# Revit family: Heater-QMARK-QWD_Series-Washdown_Corrosion_Resistant_Unit_Gen2
name_source: partatom
category: Mechanical Equipment
units: mm (PartAtom-declared; Revit-internal decimal feet)

## family parameters
Cut with Voids When Loaded = No
Host = Face
OmniClass Number = 23.75.70.17.34
OmniClass Title = Unit Heaters
Part Type = Normal
Room Calculation Point = No
Round Connector Dimension = Use Diameter
Shared = No

## types (51) — shared parameters
Apparent Load = 0 VA
Bracket = Paint - Beige
Clearance from Ceiling = 0' - 9"
Clearance from Floor = 0' - 7"
Default Elevation = 4' - 0"
Description = Corrosion Resistant Unit Heaters
Drum = Paint - Beige
Frequency = 60 Hz
Instruction Sheet Link = https://www.marleymep.com
Manufacturer = Marley® Engineered Products
Number of Poles = 1
Power Factor = 1
Product Documentation Link = https://www.marleymep.com
Product Name = QWD Series - Washdown Corrosion-Resistant Unit Heater Gen2
Product Page URL = https://www.marleymep.com
URL = https://www.marleymep.com
Version = 2020 - v1.0a
Wall Clearance = 0' - 8"
Wall Mounted Offset = 0' - 6 13/16"

## per-type parameters (varying)
| type | 2-Stage Control | Actual Supply Air Flow | Air Flow - Throw | Amps | Drum Radius | Height CM | Height WM | Motor HP | Nema Box Height | Offset From Wall | Phase | Total Heating Capacity | Voltage | Wall Mount Nema Box Offset | Watts |
| QWD02112 |  | 700 CFM | 0' - 0" | 17 A | 0' - 6 1/2" | 1' - 8 31/32" | 1' - 8 31/32" |  | 0' - 6 1/4" | 0' - 6 3/8" | 1 | 6824.0 Btu/h | 120 V | 0' - 3 25/32" | 2000 W |
| QWD02812 |  | 700 CFM | 0' - 0" | 10 A | 0' - 6 1/2" | 1' - 8 31/32" | 1' - 8 31/32" |  | 0' - 6 1/4" | 0' - 6 3/8" | 1 | 6824.0 Btu/h | 208 V | 0' - 3 25/32" | 2000 W |
| QWD02212 |  | 700 CFM | 0' - 0" | 8 A | 0' - 6 1/2" | 1' - 8 31/32" | 1' - 8 31/32" |  | 0' - 6 1/4" | 0' - 6 3/8" | 1 | 6824.0 Btu/h | 240 V | 0' - 3 25/32" | 2000 W |
| QWD03112 |  | 700 CFM | 0' - 0" | 25 A | 0' - 6 1/2" | 1' - 8 31/32" | 1' - 8 31/32" |  | 0' - 6 1/4" | 0' - 6 3/8" | 1 | 10236.0 Btu/h | 120 V | 0' - 3 25/32" | 3000 W |
| QWD03812 |  | 700 CFM | 0' - 0" | 14 A | 0' - 6 1/2" | 1' - 8 31/32" | 1' - 8 31/32" |  | 0' - 6 1/4" | 0' - 6 3/8" | 1 | 10236.0 Btu/h | 208 V | 0' - 3 25/32" | 3000 W |
| QWD03212 |  | 700 CFM | 0' - 0" | 13 A | 0' - 6 1/2" | 1' - 8 31/32" | 1' - 8 31/32" |  | 0' - 6 1/4" | 0' - 6 3/8" | 1 | 10236.0 Btu/h | 240 V | 0' - 3 25/32" | 3000 W |
| QWD03712 |  | 700 CFM | 0' - 0" | 11 A | 0' - 6 1/2" | 1' - 8 31/32" | 1' - 8 31/32" |  | 0' - 6 1/4" | 0' - 6 3/8" | 1 | 10236.0 Btu/h | 277 V | 0' - 3 25/32" | 3000 W |
| QWD03832 |  | 700 CFM | 0' - 0" | 8 A | 0' - 6 1/2" | 1' - 8 31/32" | 1' - 8 31/32" |  | 0' - 6 1/4" | 0' - 6 3/8" | 3 | 10236.0 Btu/h | 208 V | 0' - 3 25/32" | 3000 W |
| QWD03232 |  | 700 CFM | 0' - 0" | 7 A | 0' - 6 1/2" | 1' - 8 31/32" | 1' - 8 31/32" |  | 0' - 6 1/4" | 0' - 6 3/8" | 3 | 10236.0 Btu/h | 240 V | 0' - 3 25/32" | 3000 W |
| QWD03432 |  | 700 CFM | 0' - 0" | 4 A | 0' - 6 1/2" | 1' - 8 31/32" | 1' - 8 31/32" |  | 0' - 6 1/4" | 0' - 6 3/8" | 3 | 10236.0 Btu/h | 480 V | 0' - 3 25/32" | 3000 W |
| QWD05812 |  | 700 CFM | 0' - 0" | 24 A | 0' - 6 1/2" | 1' - 8 31/32" | 1' - 8 31/32" |  | 0' - 6 1/4" | 0' - 6 3/8" | 1 | 17060.0 Btu/h | 208 V | 0' - 3 25/32" | 5000 W |
| QWD05212 |  | 700 CFM | 0' - 0" | 21 A | 0' - 6 1/2" | 1' - 8 31/32" | 1' - 8 31/32" |  | 0' - 6 1/4" | 0' - 6 3/8" | 1 | 17060.0 Btu/h | 240 V | 0' - 3 25/32" | 5000 W |
| QWD05712 |  | 700 CFM | 0' - 0" | 18 A | 0' - 6 1/2" | 1' - 8 31/32" | 1' - 8 31/32" |  | 0' - 6 1/4" | 0' - 6 3/8" | 1 | 17060.0 Btu/h | 277 V | 0' - 3 25/32" | 5000 W |
| QWD05412 |  | 700 CFM | 0' - 0" | 10 A | 0' - 6 1/2" | 1' - 8 31/32" | 1' - 8 31/32" |  | 0' - 6 1/4" | 0' - 6 3/8" | 1 | 17060.0 Btu/h | 480 V | 0' - 3 25/32" | 5000 W |
| QWD05832 |  | 700 CFM | 0' - 0" | 14 A | 0' - 6 1/2" | 1' - 8 31/32" | 1' - 8 31/32" |  | 0' - 6 1/4" | 0' - 6 3/8" | 3 | 17060.0 Btu/h | 208 V | 0' - 3 25/32" | 5000 W |
| QWD05232 |  | 700 CFM | 0' - 0" | 12 A | 0' - 6 1/2" | 1' - 8 31/32" | 1' - 8 31/32" |  | 0' - 6 1/4" | 0' - 6 3/8" | 3 | 17060.0 Btu/h | 240 V | 0' - 3 25/32" | 5000 W |
| QWD05432 |  | 700 CFM | 0' - 0" | 6 A | 0' - 6 1/2" | 1' - 8 31/32" | 1' - 8 31/32" |  | 0' - 6 1/4" | 0' - 6 3/8" | 3 | 17060.0 Btu/h | 480 V | 0' - 3 25/32" | 5000 W |
| QWD07812 |  | 700 CFM | 0' - 0" | 36 A | 0' - 6 1/2" | 1' - 8 31/32" | 1' - 8 31/32" |  | 0' - 6 1/4" | 0' - 6 3/8" | 1 | 25590.0 Btu/h | 208 V | 0' - 3 25/32" | 7500 W |
| QWD07212 |  | 700 CFM | 0' - 0" | 31 A | 0' - 6 1/2" | 1' - 8 31/32" | 1' - 8 31/32" |  | 0' - 6 1/4" | 0' - 6 3/8" | 1 | 25590.0 Btu/h | 240 V | 0' - 3 25/32" | 7500 W |
| QWD07712 |  | 700 CFM | 0' - 0" | 27 A | 0' - 6 1/2" | 1' - 8 31/32" | 1' - 8 31/32" |  | 0' - 6 1/4" | 0' - 6 3/8" | 1 | 25590.0 Btu/h | 277 V | 0' - 3 25/32" | 7500 W |
| QWD07412 |  | 700 CFM | 0' - 0" | 16 A | 0' - 6 1/2" | 1' - 8 31/32" | 1' - 8 31/32" |  | 0' - 6 1/4" | 0' - 6 3/8" | 1 | 25590.0 Btu/h | 480 V | 0' - 3 25/32" | 7500 W |
| QWD07832 |  | 700 CFM | 0' - 0" | 21 A | 0' - 6 1/2" | 1' - 8 31/32" | 1' - 8 31/32" |  | 0' - 6 1/4" | 0' - 6 3/8" | 3 | 25590.0 Btu/h | 208 V | 0' - 3 25/32" | 7500 W |
| QWD07232 |  | 700 CFM | 0' - 0" | 18 A | 0' - 6 1/2" | 1' - 8 31/32" | 1' - 8 31/32" |  | 0' - 6 1/4" | 0' - 6 3/8" | 3 | 25590.0 Btu/h | 240 V | 0' - 3 25/32" | 7500 W |
| QWD07432 |  | 700 CFM | 0' - 0" | 9 A | 0' - 6 1/2" | 1' - 8 31/32" | 1' - 8 31/32" |  | 0' - 6 1/4" | 0' - 6 3/8" | 3 | 25590.0 Btu/h | 480 V | 0' - 3 25/32" | 7500 W |
| QWD10212 |  | 1450 CFM | 0' - 0" | 42 A | 0' - 6 1/2" | 1' - 8 31/32" | 1' - 8 31/32" |  | 0' - 6 1/4" | 0' - 6 3/8" | 1 | 34120.0 Btu/h | 240 V | 0' - 3 25/32" | 10000 W |
| QWD10712 |  | 1450 CFM | 0' - 0" | 36 A | 0' - 6 1/2" | 1' - 8 31/32" | 1' - 8 31/32" |  | 0' - 6 1/4" | 0' - 6 3/8" | 1 | 34120.0 Btu/h | 277 V | 0' - 3 25/32" | 10000 W |
| QWD10412 |  | 1450 CFM | 0' - 0" | 21 A | 0' - 6 1/2" | 1' - 8 31/32" | 1' - 8 31/32" |  | 0' - 6 1/4" | 0' - 6 3/8" | 1 | 34120.0 Btu/h | 480 V | 0' - 3 25/32" | 10000 W |
| QWD10832 |  | 1450 CFM | 0' - 0" | 28 A | 0' - 6 1/2" | 1' - 8 31/32" | 1' - 8 31/32" |  | 0' - 6 1/4" | 0' - 6 3/8" | 3 | 34120.0 Btu/h | 208 V | 0' - 3 25/32" | 10000 W |
| QWD10232 |  | 1450 CFM | 0' - 0" | 24 A | 0' - 6 1/2" | 1' - 8 31/32" | 1' - 8 31/32" |  | 0' - 6 1/4" | 0' - 6 3/8" | 3 | 34120.0 Btu/h | 240 V | 0' - 3 25/32" | 10000 W |
| QWD10432 |  | 1450 CFM | 0' - 0" | 12 A | 0' - 6 1/2" | 1' - 8 31/32" | 1' - 8 31/32" |  | 0' - 6 1/4" | 0' - 6 3/8" | 3 | 34120.0 Btu/h | 480 V | 0' - 3 25/32" | 10000 W |
| QWD12812 |  | 1450 CFM | 0' - 0" | 60 A | 0' - 9 7/8" | 2' - 6 7/16" | 2' - 6 7/16" |  | 0' - 8 5/16" | 0' - 8" | 1 | 42650.0 Btu/h | 208 V | 0' - 7 7/16" | 12500 W |
| QWD12212 |  | 1450 CFM | 0' - 0" | 52 A | 0' - 9 7/8" | 2' - 6 7/16" | 2' - 6 7/16" |  | 0' - 8 5/16" | 0' - 8" | 1 | 42650.0 Btu/h | 240 V | 0' - 7 7/16" | 12500 W |
| QWD12832 |  | 1450 CFM | 0' - 0" | 35 A | 0' - 9 7/8" | 2' - 6 7/16" | 2' - 6 7/16" |  | 0' - 8 5/16" | 0' - 8" | 3 | 42650.0 Btu/h | 208 V | 0' - 7 7/16" | 12500 W |
| QWD12232 |  | 1450 CFM | 0' - 0" | 30 A | 0' - 9 7/8" | 2' - 6 7/16" | 2' - 6 7/16" |  | 0' - 8 5/16" | 0' - 8" | 3 | 42650.0 Btu/h | 240 V | 0' - 7 7/16" | 12500 W |
| QWD12432 |  | 1450 CFM | 0' - 0" | 15 A | 0' - 9 7/8" | 2' - 6 7/16" | 2' - 6 7/16" |  | 0' - 8 5/16" | 0' - 8" | 3 | 42650.0 Btu/h | 480 V | 0' - 7 7/16" | 12500 W |
| QWD-234-U11L-0150I | 1A | 2400 CFM | 4' - 2" | 47 A | 0' - 9 7/8" | 2' - 6 7/16" | 2' - 6 7/16" | 0.25 | 0' - 8 5/16" | 0' - 8" | 1 | 51180.0 Btu/h | 347 V | 0' - 7 7/16" | 15000 W |
| QWD-234-U11L-0150D | 1A | 2400 CFM | 4' - 2" | 44 A | 0' - 9 7/8" | 2' - 6 7/16" | 2' - 6 7/16" | 0.25 | 0' - 8 5/16" | 0' - 8" | 3 | 51180.0 Btu/h | 208 V | 0' - 7 7/16" | 15000 W |
| QWD-234-U11L-0150K | 1A | 2400 CFM | 4' - 2" | 39 A | 0' - 9 7/8" | 2' - 6 7/16" | 2' - 6 7/16" | 0.25 | 0' - 8 5/16" | 0' - 8" | 3 | 51180.0 Btu/h | 240 V | 0' - 7 7/16" | 15000 W |
| QWD-234-U11L-0150U | 1A | 2400 CFM | 4' - 2" | 20 A | 0' - 9 7/8" | 2' - 6 7/16" | 2' - 6 7/16" | 0.25 | 0' - 8 5/16" | 0' - 8" | 3 | 51180.0 Btu/h | 480 V | 0' - 7 7/16" | 15000 W |
| QWD-234-U11L-0150Z | 1A | 2400 CFM | 4' - 2" | 16 A | 0' - 9 7/8" | 2' - 6 7/16" | 2' - 6 7/16" | 0.25 | 0' - 8 5/16" | 0' - 8" | 3 | 51180.0 Btu/h | 600 V | 0' - 7 7/16" | 15000 W |
| QWD-234-U11L-0200U | 1A | 2400 CFM | 4' - 2" | 26 A | 0' - 9 7/8" | 2' - 6 7/16" | 2' - 6 7/16" | 0.25 | 0' - 8 5/16" | 0' - 8" | 3 | 68240.0 Btu/h | 480 V | 0' - 7 7/16" | 20000 W |
| QWD-234-U11L-0200Z | 1A | 2400 CFM | 4' - 2" | 21 A | 0' - 9 7/8" | 2' - 6 7/16" | 2' - 6 7/16" | 0.25 | 0' - 8 5/16" | 0' - 8" | 3 | 68240.0 Btu/h | 600 V | 0' - 7 7/16" | 20000 W |
| QWD-234-U11A-0250U | 1B | 2400 CFM | 4' - 2" | 32 A | 0' - 9 7/8" | 2' - 6 7/16" | 2' - 6 7/16" | 0.25 | 0' - 8 5/16" | 0' - 8" | 3 | 85300.0 Btu/h | 480 V | 0' - 7 7/16" | 25000 W |
| QWD-234-U11A-0250Z | 1B | 2400 CFM | 4' - 2" | 26 A | 0' - 9 7/8" | 2' - 6 7/16" | 2' - 6 7/16" | 0.25 | 0' - 8 5/16" | 0' - 8" | 3 | 85300.0 Btu/h | 600 V | 0' - 7 7/16" | 25000 W |
| QWD-234-U11A-0300U | 1B | 2400 CFM | 4' - 2" | 38 A | 0' - 9 7/8" | 2' - 6 7/16" | 2' - 6 7/16" | 0.25 | 0' - 8 5/16" | 0' - 8" | 3 | 102360.0 Btu/h | 480 V | 0' - 7 7/16" | 30000 W |
| QWD-234-U11A-0300Z | 1B | 2400 CFM | 4' - 2" | 31 A | 0' - 9 7/8" | 2' - 6 7/16" | 2' - 6 7/16" | 0.25 | 0' - 8 5/16" | 0' - 8" | 3 | 102360.0 Btu/h | 600 V | 0' - 7 7/16" | 30000 W |
| QWD-234-U11A-0350U | 1B | 2400 CFM | 4' - 2" | 44 A | 0' - 9 7/8" | 2' - 6 7/16" | 2' - 6 7/16" | 0.25 | 0' - 8 5/16" | 0' - 8" | 3 | 119425.0 Btu/h | 480 V | 0' - 7 7/16" | 35000 W |
| QWD-234-U11A-0350Z | 1B | 2400 CFM | 4' - 2" | 35 A | 0' - 9 7/8" | 2' - 6 7/16" | 2' - 6 7/16" | 0.25 | 0' - 8 5/16" | 0' - 8" | 3 | 119425.0 Btu/h | 600 V | 0' - 7 7/16" | 35000 W |
| QWD-234-U11A-0390U | 1B | 2400 CFM | 4' - 2" | 48 A | 0' - 9 7/8" | 2' - 6 7/16" | 2' - 6 7/16" | 0.25 | 0' - 8 5/16" | 0' - 8" | 3 | 133068.0 Btu/h | 480 V | 0' - 7 7/16" | 39000 W |
| QWD-234-U11A-0390Z | 1B | 2400 CFM | 4' - 2" | 38 A | 0' - 9 7/8" | 2' - 6 7/16" | 2' - 6 7/16" | 0.25 | 0' - 8 5/16" | 0' - 8" | 3 | 133068.0 Btu/h | 600 V | 0' - 7 7/16" | 39000 W |
| QWD-234-U11A-0470Z | 1B | 2400 CFM | 4' - 2" | 47 A | 0' - 9 7/8" | 2' - 6 7/16" | 2' - 6 7/16" | 0.25 | 0' - 8 5/16" | 0' - 8" | 3 | 160370.0 Btu/h | 600 V | 0' - 7 7/16" | 47000 W |

note: column(s) folded — value = type name in every type: Model

## geometry (parser evidence)
native form markers: Sweep x19
no freeform markers — native parametric forms only
